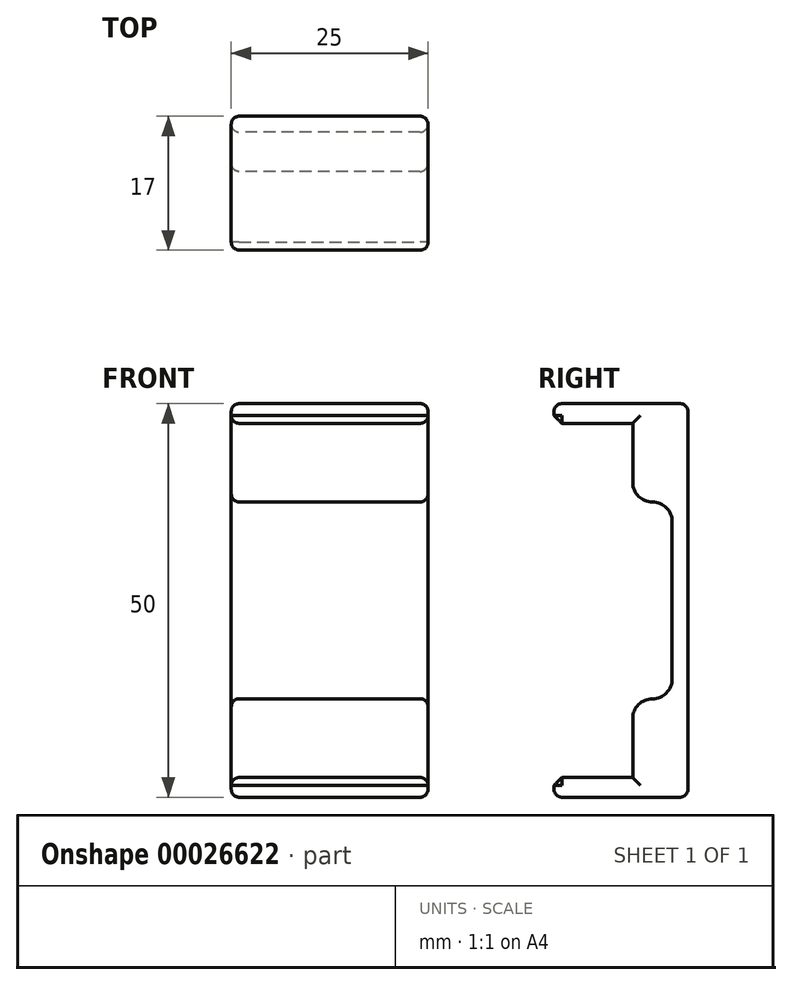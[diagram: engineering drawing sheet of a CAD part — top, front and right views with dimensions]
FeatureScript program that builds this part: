
annotation { "Feature Type Name" : "Feature", "Feature Type Description" : "" }
export const myFeature = defineFeature(function(context is Context, id is Id, definition is map)
    precondition{}
    {
        {
            var Q0;
            Q0=qCreatedBy(makeId("Right.planeOp"),FACE);
            var sketch = newSketch(context, id + "F0", { "sketchPlane" : qUnion([Q0])});
            skLineSegment(sketch, "E0.bottom", {"start": v(0, 0) * mm, "end": v(-17, 0) * mm});
            skLineSegment(sketch, "E0.top", {"start": v(0, 50) * mm, "end": v(-17, 50) * mm});
            skLineSegment(sketch, "E0.left", {"start": v(0, 0) * mm, "end": v(0, 50) * mm});
            skLineSegment(sketch, "E0.right", {"start": v(-17, 0) * mm, "end": v(-17, 50) * mm});
            skLineSegment(sketch, "E1.bottom", {"start": v(-17, 47.5) * mm, "end": v(-7, 47.5) * mm});
            skLineSegment(sketch, "E1.top", {"start": v(-17, 2.5) * mm, "end": v(-7, 2.5) * mm});
            skLineSegment(sketch, "E1.left", {"start": v(-17, 47.5) * mm, "end": v(-17, 2.5) * mm});
            skLineSegment(sketch, "E1.right", {"start": v(-7, 47.5) * mm, "end": v(-7, 2.5) * mm});
            skLineSegment(sketch, "E2", {"start": v(0, 25) * mm, "end": v(-17, 25) * mm});
            skLineSegment(sketch, "E3.bottom", {"start": v(-7, 37.5) * mm, "end": v(-2, 37.5) * mm});
            skLineSegment(sketch, "E3.top", {"start": v(-7, 12.5) * mm, "end": v(-2, 12.5) * mm});
            skLineSegment(sketch, "E3.left", {"start": v(-7, 37.5) * mm, "end": v(-7, 12.5) * mm});
            skLineSegment(sketch, "E3.right", {"start": v(-2, 37.5) * mm, "end": v(-2, 12.5) * mm});
            skSolve(sketch);
        }
        {
            var Q0;
            {var subQ4=sQuery(id+"F0.wireOp",EDGE,"E0.top");Q0=makeQuery(id+"F0.imprint","IMPRINT",FACE,{"disambiguationData":[TD([[makeQuery(id+"F0.imprint","IMPRINT",EDGE,{"derivedFrom":subQ4}),1.0]])]});}
            var Q1;
            {var subQ9=sQuery(id+"F0.wireOp",EDGE,"E0.bottom");Q1=makeQuery(id+"F0.imprint","IMPRINT",FACE,{"disambiguationData":[TD([[makeQuery(id+"F0.imprint","IMPRINT",EDGE,{"derivedFrom":subQ9}),-1.0]])]});}
            extrude(context, id + "F1", {"entities" : qUnion([Q0, Q1]), "depth" : 25 * mm});
        }
        {
            var Q0;
            Q0=makeQuery(id+"F1.opExtrude","SWEPT_EDGE",EDGE,{"disambiguationData":[OSD([sQuery(id+"F0.wireOp",EDGE,"E1.right"),sQuery(id+"F0.wireOp",EDGE,"E3.bottom"),sQuery(id+"F0.wireOp",EDGE,"E3.left")])]});
            var Q1;
            Q1=makeQuery(id+"F1.opExtrude","SWEPT_EDGE",EDGE,{"disambiguationData":[OSD([sQuery(id+"F0.wireOp",EDGE,"E1.right"),sQuery(id+"F0.wireOp",EDGE,"E3.top"),sQuery(id+"F0.wireOp",EDGE,"E3.left")])]});
            var Q2;
            Q2=makeQuery(id+"F1.opExtrude","SWEPT_EDGE",EDGE,{"disambiguationData":[OSD([sQuery(id+"F0.wireOp",EDGE,"E3.bottom"),sQuery(id+"F0.wireOp",EDGE,"E3.right")])]});
            var Q3;
            Q3=makeQuery(id+"F1.opExtrude","SWEPT_EDGE",EDGE,{"disambiguationData":[OSD([sQuery(id+"F0.wireOp",EDGE,"E3.top"),sQuery(id+"F0.wireOp",EDGE,"E3.right")])]});
            fillet(context, id + "F2", {"entities" : qUnion([Q0, Q1, Q2, Q3]), "radius" : 2.5 * mm, "tangentPropagation" : true, "allowEdgeOverflow" : false});
        }
        {
            var Q0;
            Q0=makeQuery(id+"F1.opExtrude","SWEPT_FACE",FACE,{"disambiguationData":[OSD([sQuery(id+"F0.wireOp",EDGE,"E0.left")])]});
            var Q1;
            Q1=makeQuery(id+"F1.opExtrude","CAP_FACE",FACE,{"disambiguationData":[OSD([sQuery(id+"F0.wireOp",EDGE,"E0.bottom"),sQuery(id+"F0.wireOp",EDGE,"E0.top"),sQuery(id+"F0.wireOp",EDGE,"E0.left"),sQuery(id+"F0.wireOp",EDGE,"E0.right"),sQuery(id+"F0.wireOp",EDGE,"E1.bottom"),sQuery(id+"F0.wireOp",EDGE,"E1.top"),sQuery(id+"F0.wireOp",EDGE,"E1.right"),sQuery(id+"F0.wireOp",EDGE,"E3.bottom"),sQuery(id+"F0.wireOp",EDGE,"E3.top"),sQuery(id+"F0.wireOp",EDGE,"E3.right")])],"isStart":true});
            var Q2;
            Q2=makeQuery(id+"F1.opExtrude","CAP_FACE",FACE,{"disambiguationData":[OSD([sQuery(id+"F0.wireOp",EDGE,"E0.bottom"),sQuery(id+"F0.wireOp",EDGE,"E0.top"),sQuery(id+"F0.wireOp",EDGE,"E0.left"),sQuery(id+"F0.wireOp",EDGE,"E0.right"),sQuery(id+"F0.wireOp",EDGE,"E1.bottom"),sQuery(id+"F0.wireOp",EDGE,"E1.top"),sQuery(id+"F0.wireOp",EDGE,"E1.right"),sQuery(id+"F0.wireOp",EDGE,"E3.bottom"),sQuery(id+"F0.wireOp",EDGE,"E3.top"),sQuery(id+"F0.wireOp",EDGE,"E3.right")])],"isStart":false});
            var Q3;
            Q3=makeQuery(id+"F1.opExtrude","SWEPT_FACE",FACE,{"disambiguationData":[OSD([sQuery(id+"F0.wireOp",EDGE,"E0.top")])]});
            var Q4;
            Q4=makeQuery(id+"F1.opExtrude","SWEPT_FACE",FACE,{"disambiguationData":[OSD([sQuery(id+"F0.wireOp",EDGE,"E0.bottom")])]});
            fillet(context, id + "F3", {"entities" : qUnion([Q0, Q1, Q2, Q3, Q4]), "radius" : 1 * mm, "tangentPropagation" : true, "allowEdgeOverflow" : false});
        }
        {
            var Q0;
            Q0=makeQuery(id+"F1.opExtrude","SWEPT_EDGE",EDGE,{"disambiguationData":[OSD([sQuery(id+"F0.wireOp",EDGE,"E0.right"),sQuery(id+"F0.wireOp",EDGE,"E1.bottom"),sQuery(id+"F0.wireOp",EDGE,"E1.left")])]});
            var Q1;
            Q1=makeQuery(id+"F1.opExtrude","SWEPT_EDGE",EDGE,{"disambiguationData":[OSD([sQuery(id+"F0.wireOp",EDGE,"E0.right"),sQuery(id+"F0.wireOp",EDGE,"E1.top"),sQuery(id+"F0.wireOp",EDGE,"E1.left")])]});
            chamfer(context, id + "F4", {"entities" : qUnion([Q0, Q1]), "width" : 1 * mm, "tangentPropagation" : true});
        }
    });
